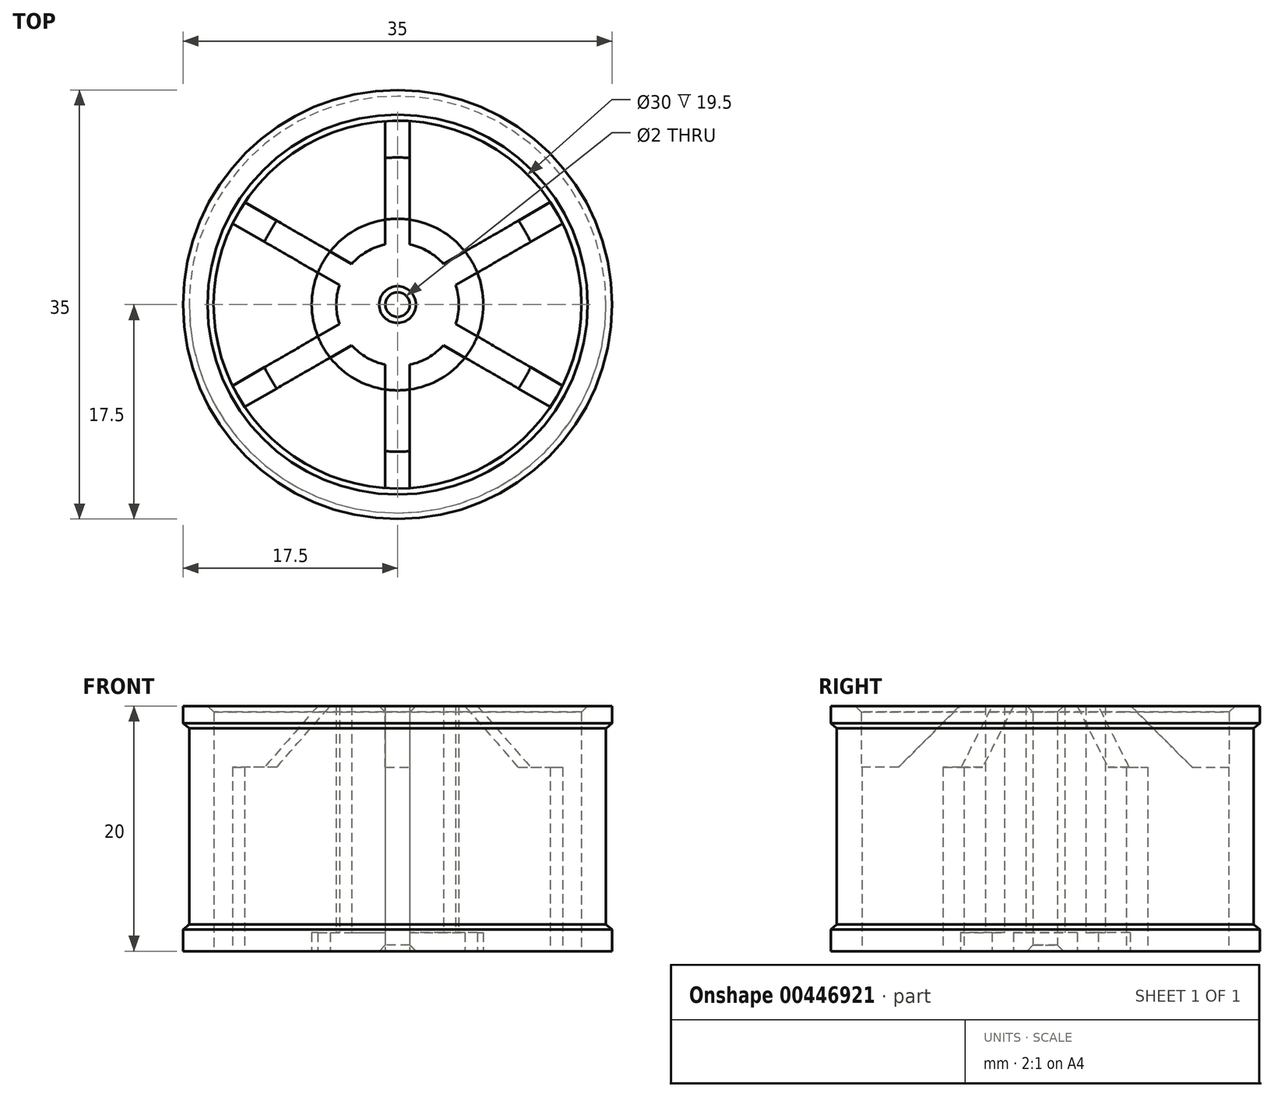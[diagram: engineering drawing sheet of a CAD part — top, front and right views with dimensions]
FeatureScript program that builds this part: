
annotation { "Feature Type Name" : "Feature", "Feature Type Description" : "" }
export const myFeature = defineFeature(function(context is Context, id is Id, definition is map)
    precondition{}
    {
        {
            var Q0;
            Q0=qCreatedBy(makeId("Top.planeOp"),FACE);
            var sketch = newSketch(context, id + "F0", { "sketchPlane" : qUnion([Q0])});
            skCircle(sketch, "E0", {"center": v(0, 0) * mm, "radius": 5 * mm});
            skCircle(sketch, "E1", {"center": v(0, 0) * mm, "radius": 1 * mm});
            skCircle(sketch, "E2", {"center": v(0, 0) * mm, "radius": 15 * mm});
            skCircle(sketch, "E3", {"center": v(0, 0) * mm, "radius": 17.5 * mm});
            skSolve(sketch);
        }
        {
            var Q0;
            Q0=makeQuery(id+"F0.imprint","IMPRINT",FACE,{"disambiguationData":[TD([[makeQuery(id+"F0.imprint","IMPRINT",EDGE,{"derivedFrom":sQuery(id+"F0.wireOp",EDGE,"E0")}),1.0]])]});
            var Q1;
            Q1=makeQuery(id+"F0.imprint","IMPRINT",FACE,{"disambiguationData":[TD([[makeQuery(id+"F0.imprint","IMPRINT",EDGE,{"derivedFrom":sQuery(id+"F0.wireOp",EDGE,"E2")}),-1.0]])]});
            extrude(context, id + "F1", {"entities" : qUnion([Q0, Q1]), "depth" : 20 * mm});
        }
        {
            var Q0;
            Q0=qCreatedBy(makeId("Top.planeOp"),FACE);
            var sketch = newSketch(context, id + "F2", { "sketchPlane" : qUnion([Q0])});
            skLineSegment(sketch, "E4.bottom", {"start": v(1, 4) * mm, "end": v(-1, 4) * mm});
            skLineSegment(sketch, "E4.top", {"start": v(1, 16) * mm, "end": v(-1, 16) * mm});
            skLineSegment(sketch, "E4.left", {"start": v(1, 4) * mm, "end": v(1, 16) * mm});
            skLineSegment(sketch, "E4.right", {"start": v(-1, 4) * mm, "end": v(-1, 16) * mm});
            skPoint(sketch, "E4.middle", {"position": v(0, 10) * mm});
            skSolve(sketch);
        }
        {
            var Q0;
            Q0 = qSketchRegion(id + "F2", true);
            extrude(context, id + "F3", {"entities" : qUnion([Q0]), "depth" : 15 * mm});
        }
        {
            var Q0;
            Q0=makeQuery(id+"F3.opExtrude","SWEPT_BODY",BODY,{"disambiguationData":[OSD([sQuery(id+"F2.wireOp",EDGE,"E4.bottom"),sQuery(id+"F2.wireOp",EDGE,"E4.top"),sQuery(id+"F2.wireOp",EDGE,"E4.left"),sQuery(id+"F2.wireOp",EDGE,"E4.right")])]});
            var Q1;
            Q1=makeQuery(id+"F1.opExtrude","SWEPT_FACE",FACE,{"disambiguationData":[OSD([sQuery(id+"F0.wireOp",EDGE,"E1")])]});
            circularPattern(context, id + "F4", {"entities" : qUnion([Q0]), "axis" : qUnion([Q1]), "angle" : 360 * degree, "instanceCount" : 6, "equalSpace" : true});
        }
        {
            var Q0;
            Q0=makeQuery(id+"F4.opPattern","COPY",BODY,{"derivedFrom":makeQuery(id+"F3.opExtrude","SWEPT_BODY",BODY,{"disambiguationData":[OSD([sQuery(id+"F2.wireOp",EDGE,"E4.bottom"),sQuery(id+"F2.wireOp",EDGE,"E4.top"),sQuery(id+"F2.wireOp",EDGE,"E4.left"),sQuery(id+"F2.wireOp",EDGE,"E4.right")])]}),"instanceName":"4"});
            var Q1;
            Q1=makeQuery(id+"F4.opPattern","COPY",BODY,{"derivedFrom":makeQuery(id+"F3.opExtrude","SWEPT_BODY",BODY,{"disambiguationData":[OSD([sQuery(id+"F2.wireOp",EDGE,"E4.bottom"),sQuery(id+"F2.wireOp",EDGE,"E4.top"),sQuery(id+"F2.wireOp",EDGE,"E4.left"),sQuery(id+"F2.wireOp",EDGE,"E4.right")])]}),"instanceName":"1"});
            var Q2;
            Q2=makeQuery(id+"F4.opPattern","COPY",BODY,{"derivedFrom":makeQuery(id+"F3.opExtrude","SWEPT_BODY",BODY,{"disambiguationData":[OSD([sQuery(id+"F2.wireOp",EDGE,"E4.bottom"),sQuery(id+"F2.wireOp",EDGE,"E4.top"),sQuery(id+"F2.wireOp",EDGE,"E4.left"),sQuery(id+"F2.wireOp",EDGE,"E4.right")])]}),"instanceName":"2"});
            var Q3;
            Q3=makeQuery(id+"F4.opPattern","COPY",BODY,{"derivedFrom":makeQuery(id+"F3.opExtrude","SWEPT_BODY",BODY,{"disambiguationData":[OSD([sQuery(id+"F2.wireOp",EDGE,"E4.bottom"),sQuery(id+"F2.wireOp",EDGE,"E4.top"),sQuery(id+"F2.wireOp",EDGE,"E4.left"),sQuery(id+"F2.wireOp",EDGE,"E4.right")])]}),"instanceName":"3"});
            var Q4;
            Q4=makeQuery(id+"F1.opExtrude","SWEPT_BODY",BODY,{"disambiguationData":[OSD([sQuery(id+"F0.wireOp",EDGE,"E0"),sQuery(id+"F0.wireOp",EDGE,"E1")])]});
            var Q5;
            Q5=makeQuery(id+"F1.opExtrude","SWEPT_BODY",BODY,{"disambiguationData":[OSD([sQuery(id+"F0.wireOp",EDGE,"E2"),sQuery(id+"F0.wireOp",EDGE,"E3")])]});
            var Q6;
            Q6=makeQuery(id+"F3.opExtrude","SWEPT_BODY",BODY,{"disambiguationData":[OSD([sQuery(id+"F2.wireOp",EDGE,"E4.bottom"),sQuery(id+"F2.wireOp",EDGE,"E4.top"),sQuery(id+"F2.wireOp",EDGE,"E4.left"),sQuery(id+"F2.wireOp",EDGE,"E4.right")])]});
            var Q7;
            Q7=makeQuery(id+"F4.opPattern","COPY",BODY,{"derivedFrom":makeQuery(id+"F3.opExtrude","SWEPT_BODY",BODY,{"disambiguationData":[OSD([sQuery(id+"F2.wireOp",EDGE,"E4.bottom"),sQuery(id+"F2.wireOp",EDGE,"E4.top"),sQuery(id+"F2.wireOp",EDGE,"E4.left"),sQuery(id+"F2.wireOp",EDGE,"E4.right")])]}),"instanceName":"5"});
            booleanBodies(context, id + "F5", {"operationType" : BooleanOperationType.UNION, "tools" : qUnion([Q0, Q1, Q2, Q3, Q4, Q5, Q6, Q7])});
        }
        {
            var Q0;
            Q0=makeQuery(id+"F5.opBoolean","INTERSECT",EDGE,{"derivedFrom":[makeQuery(id+"F1.opExtrude","SWEPT_FACE",FACE,{"disambiguationData":[OSD([sQuery(id+"F0.wireOp",EDGE,"E0")])]}),makeQuery(id+"F4.opPattern","COPY",FACE,{"derivedFrom":makeQuery(id+"F3.opExtrude","CAP_FACE",FACE,{"disambiguationData":[OSD([sQuery(id+"F2.wireOp",EDGE,"E4.bottom"),sQuery(id+"F2.wireOp",EDGE,"E4.top"),sQuery(id+"F2.wireOp",EDGE,"E4.left"),sQuery(id+"F2.wireOp",EDGE,"E4.right")])],"isStart":false}),"instanceName":"2"})]});
            var Q1;
            Q1=makeQuery(id+"F5.opBoolean","INTERSECT",EDGE,{"derivedFrom":[makeQuery(id+"F1.opExtrude","SWEPT_FACE",FACE,{"disambiguationData":[OSD([sQuery(id+"F0.wireOp",EDGE,"E0")])]}),makeQuery(id+"F4.opPattern","COPY",FACE,{"derivedFrom":makeQuery(id+"F3.opExtrude","CAP_FACE",FACE,{"disambiguationData":[OSD([sQuery(id+"F2.wireOp",EDGE,"E4.bottom"),sQuery(id+"F2.wireOp",EDGE,"E4.top"),sQuery(id+"F2.wireOp",EDGE,"E4.left"),sQuery(id+"F2.wireOp",EDGE,"E4.right")])],"isStart":false}),"instanceName":"1"})]});
            var Q2;
            Q2=makeQuery(id+"F5.opBoolean","INTERSECT",EDGE,{"derivedFrom":[makeQuery(id+"F1.opExtrude","SWEPT_FACE",FACE,{"disambiguationData":[OSD([sQuery(id+"F0.wireOp",EDGE,"E0")])]}),makeQuery(id+"F3.opExtrude","CAP_FACE",FACE,{"disambiguationData":[OSD([sQuery(id+"F2.wireOp",EDGE,"E4.bottom"),sQuery(id+"F2.wireOp",EDGE,"E4.top"),sQuery(id+"F2.wireOp",EDGE,"E4.left"),sQuery(id+"F2.wireOp",EDGE,"E4.right")])],"isStart":false})]});
            var Q3;
            Q3=makeQuery(id+"F5.opBoolean","INTERSECT",EDGE,{"derivedFrom":[makeQuery(id+"F1.opExtrude","SWEPT_FACE",FACE,{"disambiguationData":[OSD([sQuery(id+"F0.wireOp",EDGE,"E0")])]}),makeQuery(id+"F4.opPattern","COPY",FACE,{"derivedFrom":makeQuery(id+"F3.opExtrude","CAP_FACE",FACE,{"disambiguationData":[OSD([sQuery(id+"F2.wireOp",EDGE,"E4.bottom"),sQuery(id+"F2.wireOp",EDGE,"E4.top"),sQuery(id+"F2.wireOp",EDGE,"E4.left"),sQuery(id+"F2.wireOp",EDGE,"E4.right")])],"isStart":false}),"instanceName":"5"})]});
            var Q4;
            Q4=makeQuery(id+"F5.opBoolean","INTERSECT",EDGE,{"derivedFrom":[makeQuery(id+"F1.opExtrude","SWEPT_FACE",FACE,{"disambiguationData":[OSD([sQuery(id+"F0.wireOp",EDGE,"E0")])]}),makeQuery(id+"F4.opPattern","COPY",FACE,{"derivedFrom":makeQuery(id+"F3.opExtrude","CAP_FACE",FACE,{"disambiguationData":[OSD([sQuery(id+"F2.wireOp",EDGE,"E4.bottom"),sQuery(id+"F2.wireOp",EDGE,"E4.top"),sQuery(id+"F2.wireOp",EDGE,"E4.left"),sQuery(id+"F2.wireOp",EDGE,"E4.right")])],"isStart":false}),"instanceName":"4"})]});
            var Q5;
            Q5=makeQuery(id+"F5.opBoolean","INTERSECT",EDGE,{"derivedFrom":[makeQuery(id+"F1.opExtrude","SWEPT_FACE",FACE,{"disambiguationData":[OSD([sQuery(id+"F0.wireOp",EDGE,"E0")])]}),makeQuery(id+"F4.opPattern","COPY",FACE,{"derivedFrom":makeQuery(id+"F3.opExtrude","CAP_FACE",FACE,{"disambiguationData":[OSD([sQuery(id+"F2.wireOp",EDGE,"E4.bottom"),sQuery(id+"F2.wireOp",EDGE,"E4.top"),sQuery(id+"F2.wireOp",EDGE,"E4.left"),sQuery(id+"F2.wireOp",EDGE,"E4.right")])],"isStart":false}),"instanceName":"3"})]});
            chamfer(context, id + "F6", {"entities" : qUnion([Q0, Q1, Q2, Q3, Q4, Q5]), "width" : 7 * mm, "tangentPropagation" : true});
        }
        {
            var Q0;
            Q0=qCreatedBy(makeId("Front.planeOp"),FACE);
            var sketch = newSketch(context, id + "F7", { "sketchPlane" : qUnion([Q0])});
            skLineSegment(sketch, "E5", {"start": v(-20.06, 20.74) * mm, "end": v(-17, 18.17) * mm});
            skLineSegment(sketch, "E6", {"start": v(-17, 18.17) * mm, "end": v(-17, 2.17) * mm});
            skLineSegment(sketch, "E7", {"start": v(-17, 2.17) * mm, "end": v(-20.06, -0.4) * mm});
            skLineSegment(sketch, "E8", {"start": v(-20.06, -0.4) * mm, "end": v(-20.06, 20.74) * mm});
            skSolve(sketch);
        }
        {
            var Q0;
            Q0 = qSketchRegion(id + "F7", true);
            var Q1;
            Q1=makeQuery(id+"F1.opExtrude","CAP_EDGE",EDGE,{"disambiguationData":[OSD([sQuery(id+"F0.wireOp",EDGE,"E1")])],"isStart":false});
            revolve(context, id + "F8", {"operationType" : NewBodyOperationType.REMOVE, "entities" : qUnion([Q0]), "axis" : qUnion([Q1]), "revolveType" : RevolveType.FULL, "oppositeDirection" : true});
        }
        {
            var Q0;
            Q0=makeQuery(id+"F1.opExtrude","CAP_EDGE",EDGE,{"disambiguationData":[OSD([sQuery(id+"F0.wireOp",EDGE,"E1")])],"isStart":false});
            var Q1;
            Q1=makeQuery(id+"F1.opExtrude","CAP_EDGE",EDGE,{"disambiguationData":[OSD([sQuery(id+"F0.wireOp",EDGE,"E2")])],"isStart":false});
            chamfer(context, id + "F9", {"entities" : qUnion([Q0, Q1]), "width" : 0.5 * mm, "tangentPropagation" : true});
        }
        {
            var Q0;
            {var subQ0=makeQuery(id+"F3.opExtrude","CAP_FACE",FACE,{"disambiguationData":[OSD([sQuery(id+"F2.wireOp",EDGE,"E4.bottom"),sQuery(id+"F2.wireOp",EDGE,"E4.top"),sQuery(id+"F2.wireOp",EDGE,"E4.left"),sQuery(id+"F2.wireOp",EDGE,"E4.right")])],"isStart":true});Q0=makeQuery(id+"F5.opBoolean","MERGE",FACE,{"derivedFrom":[makeQuery(id+"F1.opExtrude","CAP_FACE",FACE,{"disambiguationData":[OSD([sQuery(id+"F0.wireOp",EDGE,"E0"),sQuery(id+"F0.wireOp",EDGE,"E1")])],"isStart":true}),makeQuery(id+"F1.opExtrude","CAP_FACE",FACE,{"disambiguationData":[OSD([sQuery(id+"F0.wireOp",EDGE,"E2"),sQuery(id+"F0.wireOp",EDGE,"E3")])],"isStart":true}),subQ0,makeQuery(id+"F4.opPattern","COPY",FACE,{"derivedFrom":subQ0,"instanceName":"1"}),makeQuery(id+"F4.opPattern","COPY",FACE,{"derivedFrom":subQ0,"instanceName":"2"}),makeQuery(id+"F4.opPattern","COPY",FACE,{"derivedFrom":subQ0,"instanceName":"3"}),makeQuery(id+"F4.opPattern","COPY",FACE,{"derivedFrom":subQ0,"instanceName":"4"}),makeQuery(id+"F4.opPattern","COPY",FACE,{"derivedFrom":subQ0,"instanceName":"5"})]});}
            var sketch = newSketch(context, id + "F10", { "sketchPlane" : qUnion([Q0])});
            skCircle(sketch, "E9", {"center": v(0, 0) * mm, "radius": 3.5 * mm});
            skCircle(sketch, "E10", {"center": v(0, 0) * mm, "radius": 7 * mm});
            skSolve(sketch);
        }
        {
            var Q0;
            Q0 = qSketchRegion(id + "F10", true);
            var Q1;
            {var subQ0=sQuery(id+"F10.wireOp",EDGE,"E10");var subQ1=sQuery(id+"F2.wireOp",EDGE,"E4.left");var subQ2=makeQuery(id+"F4.opPattern","COPY",EDGE,{"derivedFrom":makeQuery(id+"F3.opExtrude","CAP_EDGE",EDGE,{"disambiguationData":[OSD([subQ1])],"isStart":true}),"instanceName":"3"});var subQ3=makeQuery(id+"F10.imprint","INTERSECT",VERTEX,{"derivedFrom":[subQ2,subQ0]});Q1=makeQuery(id+"F10.imprint","IMPRINT",FACE,{"disambiguationData":[TD([[makeQuery(id+"F10.imprint","IMPRINT",EDGE,{"disambiguationData":[TD([[subQ3,-1.0]])],"derivedFrom":subQ0}),1.0]])]});}
            extrude(context, id + "F11", {"entities" : qUnion([Q0, Q1]), "operationType" : NewBodyOperationType.ADD, "oppositeDirection" : true, "depth" : 1.5 * mm});
        }
        {
            var Q0;
            Q0=makeQuery(id+"F1.opExtrude","CAP_EDGE",EDGE,{"disambiguationData":[OSD([sQuery(id+"F0.wireOp",EDGE,"E1")])],"isStart":true});
            chamfer(context, id + "F12", {"entities" : qUnion([Q0]), "width" : 0.5 * mm, "tangentPropagation" : true});
        }
    });
